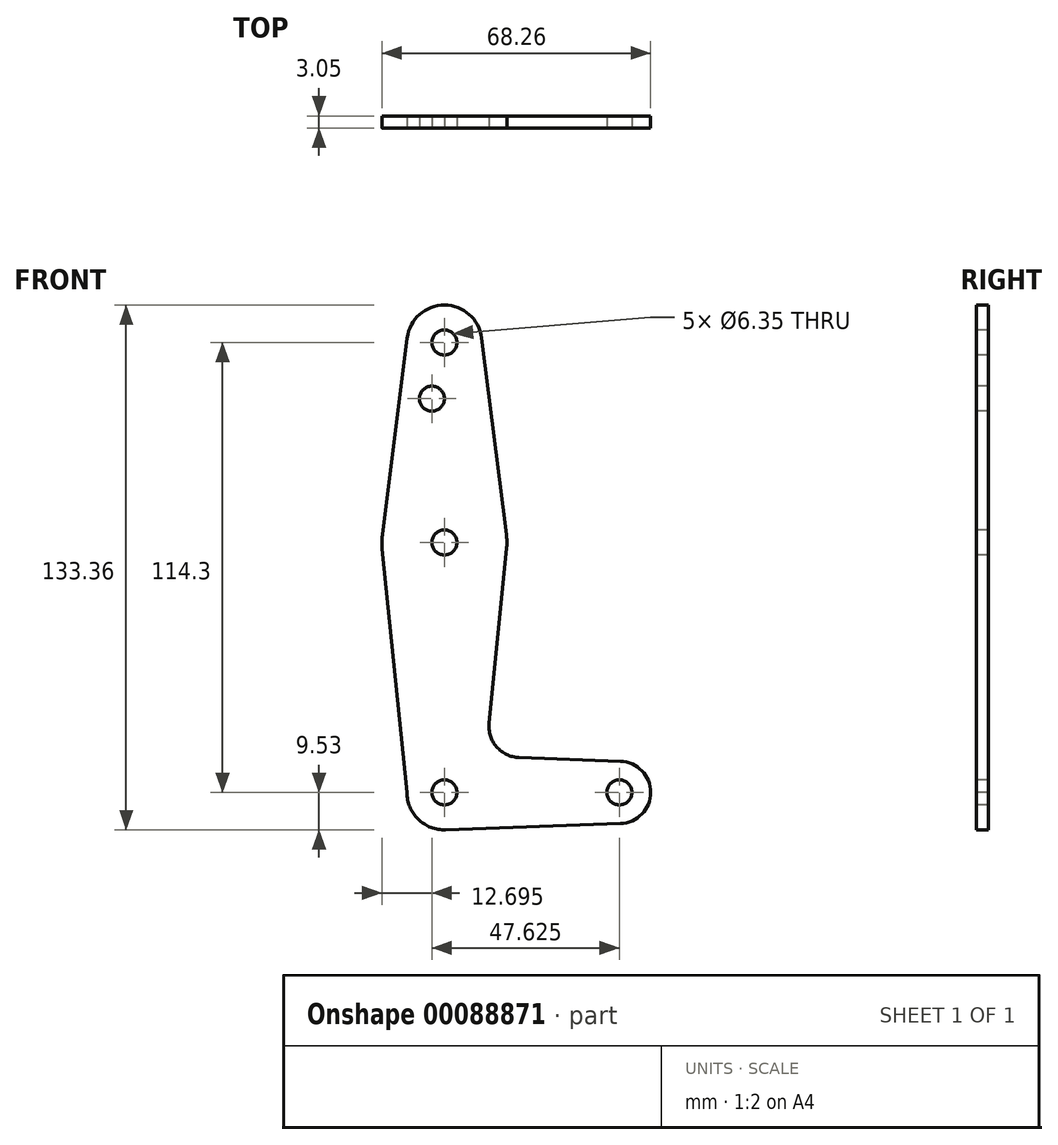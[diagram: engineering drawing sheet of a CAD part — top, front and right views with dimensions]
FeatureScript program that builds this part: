
annotation { "Feature Type Name" : "Feature", "Feature Type Description" : "" }
export const myFeature = defineFeature(function(context is Context, id is Id, definition is map)
    precondition{}
    {
        {
            var Q0;
            Q0=qCreatedBy(makeId("Front.planeOp"),FACE);
            var sketch = newSketch(context, id + "F0", { "sketchPlane" : qUnion([Q0])});
            skLineSegment(sketch, "E0", {"start": v(0, 0) * mm, "end": v(0, 114.3) * mm, "construction": true});
            skLineSegment(sketch, "E1", {"start": v(0, 0) * mm, "end": v(44.45, 0) * mm, "construction": true});
            skCircle(sketch, "E2", {"center": v(0, 114.3) * mm, "radius": 9.53 * mm});
            skCircle(sketch, "E3", {"center": v(0, 0) * mm, "radius": 9.53 * mm});
            skCircle(sketch, "E4", {"center": v(44.45, 0) * mm, "radius": 7.94 * mm});
            skCircle(sketch, "E5", {"center": v(0, 63.5) * mm, "radius": 15.88 * mm});
            skLineSegment(sketch, "E6", {"start": v(44.45, 0) * mm, "end": v(44.45, 7.94) * mm, "construction": true});
            skLineSegment(sketch, "E7", {"start": v(18.97, 8.85) * mm, "end": v(44.73, 7.93) * mm});
            skLineSegment(sketch, "E8", {"start": v(0.34, -9.52) * mm, "end": v(44.73, -7.93) * mm});
            skLineSegment(sketch, "E9", {"start": v(-9.45, 115.5) * mm, "end": v(-15.75, 65.48) * mm});
            skLineSegment(sketch, "E10", {"start": v(9.45, 115.5) * mm, "end": v(15.75, 65.48) * mm});
            skLineSegment(sketch, "E11", {"start": v(-9.52, 0) * mm, "end": v(-15.8, 61.9) * mm});
            skLineSegment(sketch, "E12", {"start": v(11.34, 17.6) * mm, "end": v(15.8, 61.91) * mm});
            skCircle(sketch, "E13", {"center": v(0, 114.3) * mm, "radius": 3.18 * mm});
            skCircle(sketch, "E14", {"center": v(0, 63.5) * mm, "radius": 3.17 * mm});
            skCircle(sketch, "E15", {"center": v(0, 0) * mm, "radius": 3.18 * mm});
            skCircle(sketch, "E16", {"center": v(44.45, 0) * mm, "radius": 3.18 * mm});
            skCircle(sketch, "E17", {"center": v(-3.17, 100.03) * mm, "radius": 3.18 * mm});
            skArc(sketch, "E18.filletArc", {"start": v(11.34, 17.6) * mm, "mid": v(13.26, 11.57) * mm, "end": v(18.97, 8.85) * mm});
            skSolve(sketch);
        }
        {
            var Q0;
            Q0 = qSketchRegion(id + "F0", true);
            var Q1;
            {var subQ1=sQuery(id+"F0.wireOp",EDGE,"E9");Q1=makeQuery(id+"F0.imprint","IMPRINT",FACE,{"disambiguationData":[TD([[makeQuery(id+"F0.imprint","IMPRINT",EDGE,{"derivedFrom":subQ1}),1.0]])]});}
            extrude(context, id + "F1", {"entities" : qUnion([Q0, Q1]), "oppositeDirection" : true, "depth" : 3.05 * mm});
        }
    });
